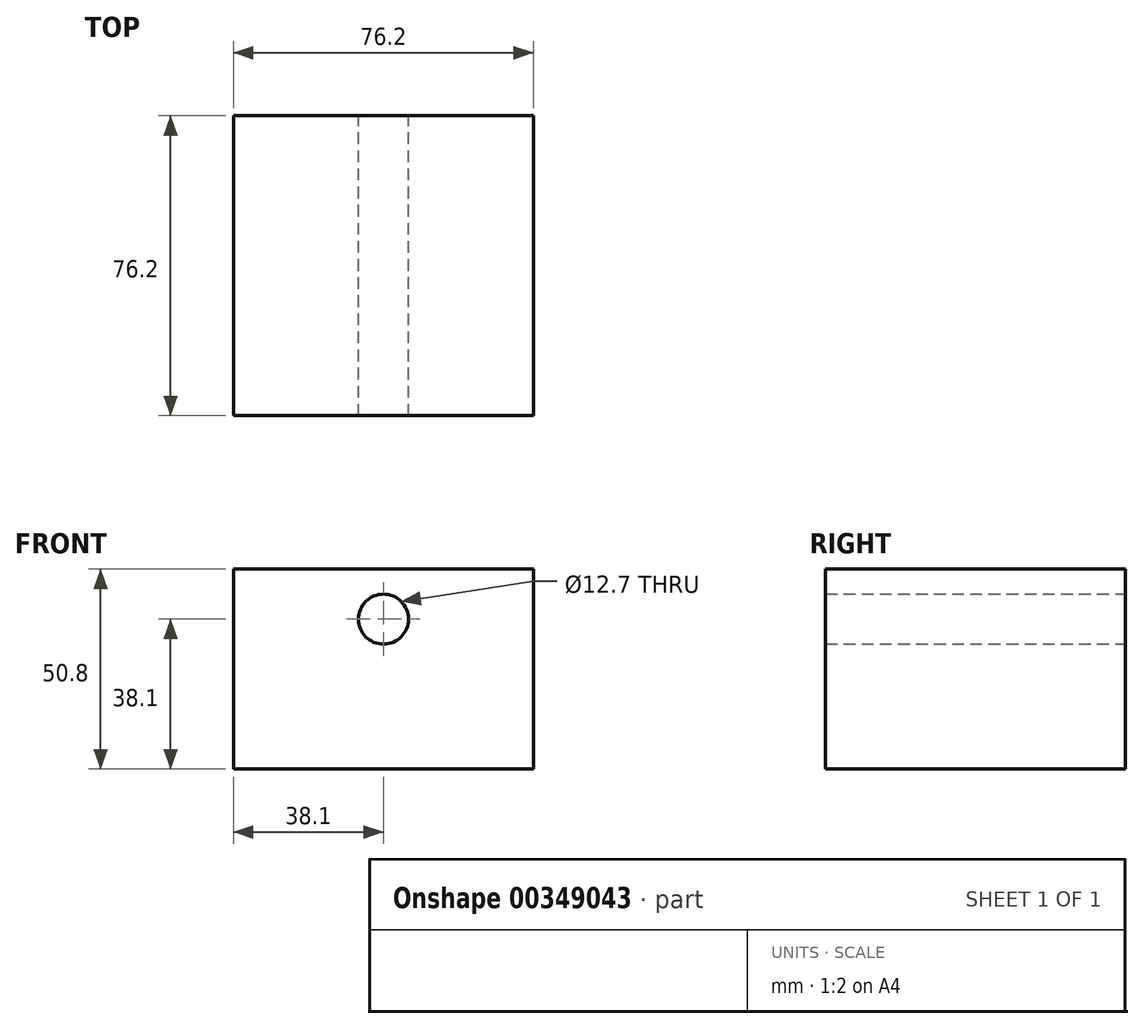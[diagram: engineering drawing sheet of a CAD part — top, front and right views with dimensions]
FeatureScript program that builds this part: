
annotation { "Feature Type Name" : "Feature", "Feature Type Description" : "" }
export const myFeature = defineFeature(function(context is Context, id is Id, definition is map)
    precondition{}
    {
        {
            var Q0;
            Q0=qCreatedBy(makeId("Top.planeOp"),FACE);
            var sketch = newSketch(context, id + "F0", { "sketchPlane" : qUnion([Q0])});
            skLineSegment(sketch, "E0.bottom", {"start": v(-38.1, 38.1) * mm, "end": v(38.1, 38.1) * mm});
            skLineSegment(sketch, "E0.top", {"start": v(-38.1, -38.1) * mm, "end": v(38.1, -38.1) * mm});
            skLineSegment(sketch, "E0.left", {"start": v(-38.1, 38.1) * mm, "end": v(-38.1, -38.1) * mm});
            skLineSegment(sketch, "E0.right", {"start": v(38.1, 38.1) * mm, "end": v(38.1, -38.1) * mm});
            skPoint(sketch, "E0.middle", {"position": v(0, 0) * mm});
            skSolve(sketch);
        }
        {
            var Q0;
            Q0=makeQuery(id+"F0.imprint","IMPRINT",FACE,{"disambiguationData":[TD([[makeQuery(id+"F0.imprint","IMPRINT",EDGE,{"derivedFrom":sQuery(id+"F0.wireOp",EDGE,"E0.bottom")}),-1.0]])]});
            extrude(context, id + "F1", {"entities" : qUnion([Q0]), "endBound" : BoundingType.SYMMETRIC, "depth" : 50.8 * mm});
        }
        {
            var Q0;
            Q0=makeQuery(id+"F1.opExtrude","SWEPT_FACE",FACE,{"disambiguationData":[OSD([sQuery(id+"F0.wireOp",EDGE,"E0.bottom")])]});
            var sketch = newSketch(context, id + "F2", { "sketchPlane" : qUnion([Q0])});
            skCircle(sketch, "E1", {"center": v(0, 12.7) * mm, "radius": 6.35 * mm});
            skSolve(sketch);
        }
        {
            var Q0;
            Q0=makeQuery(id+"F2.imprint","IMPRINT",FACE,{"disambiguationData":[TD([[makeQuery(id+"F2.imprint","IMPRINT",EDGE,{"derivedFrom":sQuery(id+"F2.wireOp",EDGE,"E1")}),1.0]])]});
            extrude(context, id + "F3", {"entities" : qUnion([Q0]), "operationType" : NewBodyOperationType.REMOVE, "endBound" : BoundingType.THROUGH_ALL, "oppositeDirection" : true, "depth" : 25.4 * mm});
        }
    });
